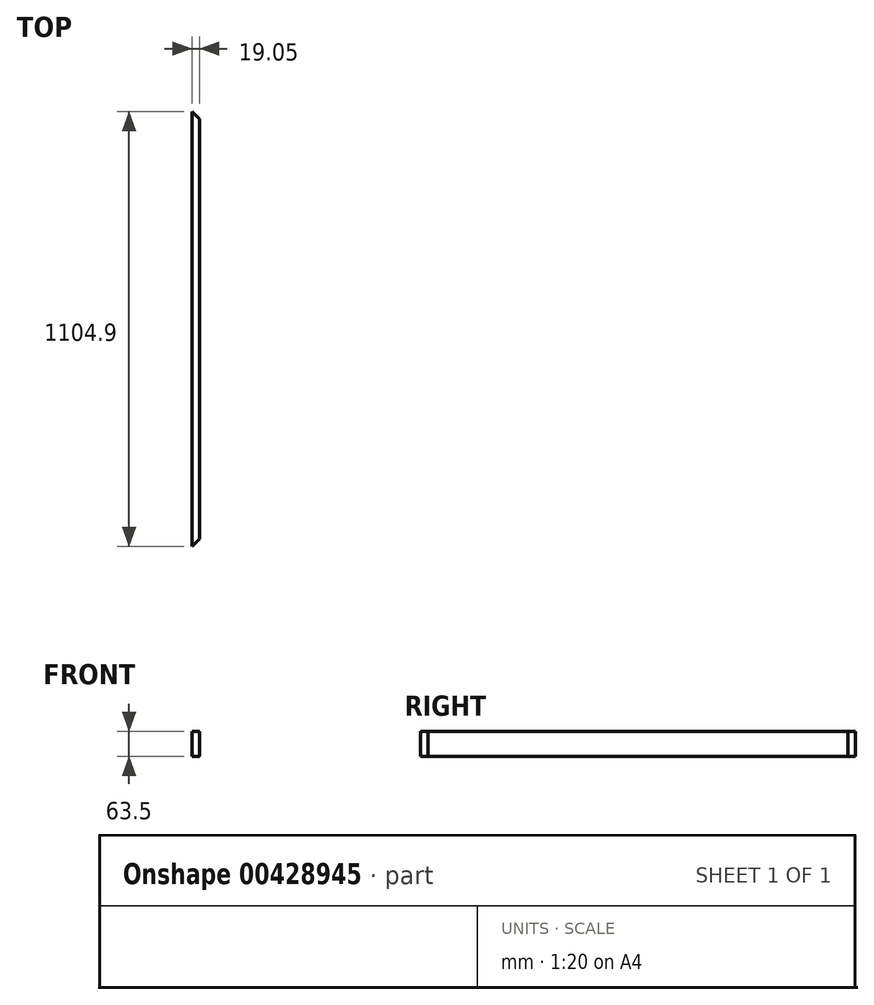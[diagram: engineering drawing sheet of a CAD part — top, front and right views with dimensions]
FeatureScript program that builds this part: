
annotation { "Feature Type Name" : "Feature", "Feature Type Description" : "" }
export const myFeature = defineFeature(function(context is Context, id is Id, definition is map)
    precondition{}
    {
        {
            var Q0;
            Q0=qCreatedBy(makeId("Right.planeOp"),FACE);
            var sketch = newSketch(context, id + "F0", { "sketchPlane" : qUnion([Q0])});
            skLineSegment(sketch, "E0.bottom", {"start": v(-1001.58, 24.62) * mm, "end": v(103.32, 24.62) * mm});
            skLineSegment(sketch, "E0.top", {"start": v(-1001.58, -38.88) * mm, "end": v(103.32, -38.88) * mm});
            skLineSegment(sketch, "E0.left", {"start": v(-1001.58, 24.62) * mm, "end": v(-1001.58, -38.88) * mm});
            skLineSegment(sketch, "E0.right", {"start": v(103.32, 24.62) * mm, "end": v(103.32, -38.88) * mm});
            skSolve(sketch);
        }
        {
            var Q0;
            Q0=makeQuery(id+"F0.imprint","IMPRINT",FACE,{"disambiguationData":[TD([[makeQuery(id+"F0.imprint","IMPRINT",EDGE,{"derivedFrom":sQuery(id+"F0.wireOp",EDGE,"E0.bottom")}),-1.0]])]});
            extrude(context, id + "F1", {"entities" : qUnion([Q0]), "depth" : 19.05 * mm});
        }
        {
            var Q0;
            Q0=makeQuery(id+"F1.opExtrude","CAP_EDGE",EDGE,{"disambiguationData":[OSD([sQuery(id+"F0.wireOp",EDGE,"E0.left")])],"isStart":false});
            var Q1;
            Q1=makeQuery(id+"F1.opExtrude","CAP_EDGE",EDGE,{"disambiguationData":[OSD([sQuery(id+"F0.wireOp",EDGE,"E0.right")])],"isStart":false});
            chamfer(context, id + "F2", {"entities" : qUnion([Q0, Q1]), "width" : 19.05 * mm, "tangentPropagation" : true});
        }
    });
